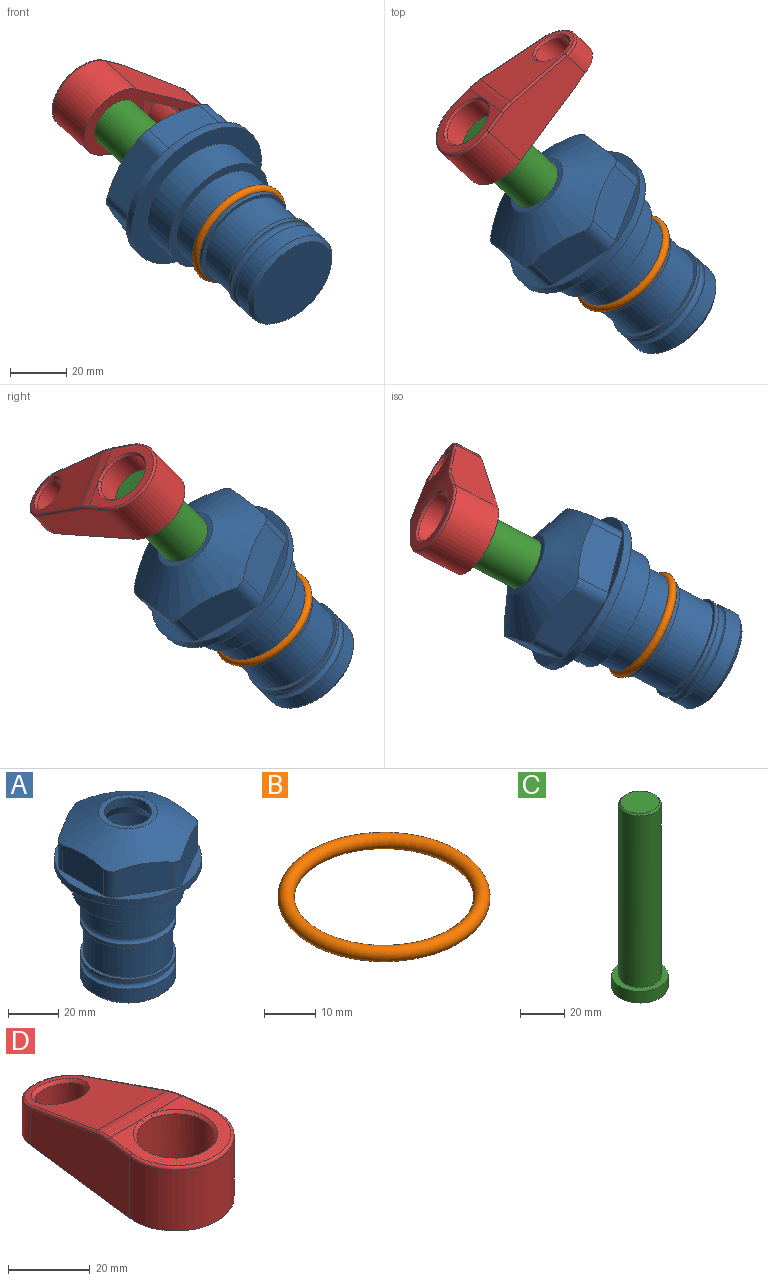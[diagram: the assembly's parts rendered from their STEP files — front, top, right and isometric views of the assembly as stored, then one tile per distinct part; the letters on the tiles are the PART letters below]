
ASSEMBLY  parts=4 mates=3
PART A: 36 faces, bbox 58.7x58.7x81 mm
  f0: cylinder r=17.78mm len=35.56mm, axis (0,0,1), area 1670.8mm2, adj f23,f24,f31
  f1: cylinder r=19.05mm len=38.1mm, axis (0,0,1), area 1191.9mm2, adj f26,f27,f30
  f2: plane 58.66x58.66mm, normal (0,0,-1), area 1150.6mm2, adj f3,f28
  f3: cylinder r=29.33mm len=58.66mm, axis (0,0,-1), area 585.1mm2, adj f2,f4
  f4: plane 58.66x58.66mm, normal (0,0,1), area 475.9mm2, adj f3,f5,f6,f7,f8,f9,f10,f11
  f5: plane 20.32x14.34mm, normal (-0.5,0.87,0), area 324.4mm2, adj f4,f15,f16,f17
  f6: plane 20.32x14.34mm, normal (0.5,0.87,0), area 324.4mm2, adj f4,f14,f15,f17
  f7: plane 23.48x14.34mm, normal (1,0,0), area 324.4mm2, adj f4,f13,f14,f17
  f8: plane 20.32x14.34mm, normal (0.5,-0.87,0), area 324.4mm2, adj f4,f12,f13,f17
  f9: plane 20.32x14.34mm, normal (-0.5,-0.87,0), area 324.4mm2, adj f4,f11,f12,f17
  f10: plane 23.48x14.34mm, normal (-1,0,0), area 324.4mm2, adj f4,f11,f16,f17
  f11: cylinder r=5.08mm len=12.85mm, axis (0,0,-1), area 67.2mm2, adj f4,f9,f10,f17
  f12: cylinder r=5.08mm len=12.85mm, axis (0,0,-1), area 67.2mm2, adj f4,f8,f9,f17
  f13: cylinder r=5.08mm len=12.85mm, axis (0,0,-1), area 67.2mm2, adj f4,f7,f8,f17
  f14: cylinder r=5.08mm len=12.85mm, axis (0,0,-1), area 67.2mm2, adj f4,f6,f7,f17
  f15: cylinder r=5.08mm len=12.85mm, axis (0,0,-1), area 67.2mm2, adj f4,f5,f6,f17
  f16: cylinder r=5.08mm len=12.85mm, axis (0,0,-1), area 67.2mm2, adj f4,f5,f10,f17
  f17: cone r=11.73mm half-angle=60deg, axis (0,0,-1), area 2071.8mm2, adj f5,f6,f7,f8,f9,f10,f11,f12
  f18: plane 23.46x23.46mm, normal (0,0,1), area 147.4mm2, adj f17,f35
  f19: plane 34.93x34.93mm, normal (0,0,-1), area 958mm2, adj f29
  f20: cylinder r=19.05mm len=38.1mm, axis (0,0,1), area 760.1mm2, adj f21,f29
  f21: torus R=19.05mm, axis (0,0,1), area 565.3mm2, adj f20,f22
  f22: cylinder r=19.05mm len=38.1mm, axis (0,0,1), area 190mm2, adj f21,f23
  f23: plane 38.1x38.1mm, normal (0,0,1), area 146.9mm2, adj f0,f22
  f24: plane 38.1x38.1mm, normal (0,0,-1), area 146.9mm2, adj f0,f25
  f25: cylinder r=19.05mm len=38.1mm, axis (0,0,1), area 190mm2, adj f24,f26
  f26: torus R=19.05mm, axis (0,0,1), area 565.3mm2, adj f1,f25
  f27: plane 44.45x44.45mm, normal (0,0,-1), area 411.7mm2, adj f1,f28
  f28: cylinder r=22.23mm len=44.45mm, axis (0,0,1), area 1773.5mm2, adj f2,f27
  f29: cone r=19.05mm half-angle=45deg, axis (0,0,1), area 257.5mm2, adj f19,f20
  f30: cylinder r=3.17mm len=6.75mm, axis (-1,0,0), area 128mm2, adj f1,f33
  f31: cylinder r=3.17mm len=6.35mm, axis (-1,0,0), area 102.5mm2, adj f0,f33
  f32: plane 25.4x25.4mm, normal (0,0,1), area 506.7mm2, adj f33
  f33: cylinder r=12.7mm len=66.42mm, axis (0,0,-1), area 5236.2mm2, adj f30,f31,f32,f34
  f34: cone r=9.53mm half-angle=30deg, axis (0,0,-1), area 443.4mm2, adj f33,f35
  f35: cylinder r=9.53mm len=19.05mm, axis (0,0,-1), area 240.9mm2, adj f18,f34
PART B: 1 faces, bbox 44.7x44.7x3.2 mm
  f0: torus R=19.05mm, axis (0,0,1), area 1193.9mm2
PART C: 6 faces, bbox 25.4x25.4x101.6 mm
  f0: plane 17.46x17.46mm, normal (0,0,1), area 239.5mm2, adj f5
  f1: plane 25.4x25.4mm, normal (0,0,-1), area 506.7mm2, adj f2
  f2: cylinder r=12.7mm len=25.4mm, axis (0,0,1), area 506.7mm2, adj f1,f3
  f3: plane 25.4x25.4mm, normal (0,0,1), area 221.7mm2, adj f2,f4
  f4: cylinder r=9.53mm len=94.46mm, axis (0,0,1), area 5653mm2, adj f3,f5
  f5: cone r=8.73mm half-angle=45deg, axis (0,0,-1), area 64.4mm2, adj f0,f4
PART D: 31 faces, bbox 31.7x65.5x19.8 mm
  f0: plane 39.12x18.26mm, normal (0.99,0.12,0), area 612.2mm2, adj f1,f4,f7,f11,f13,f15
  f1: cylinder r=9.53mm len=18.91mm, axis (0,0,-1), area 296.1mm2, adj f0,f2,f7,f17
  f2: plane 39.12x18.26mm, normal (-0.99,0.12,0), area 612.2mm2, adj f1,f4,f7,f12,f14,f16
  f3: cylinder r=6.35mm len=12.7mm, axis (0,0,-1), area 362.4mm2, adj f7,f18
  f4: cylinder r=14.29mm len=28.58mm, axis (0,0,-1), area 882.2mm2, adj f0,f2,f7,f10
  f5: cylinder r=9.53mm len=19.05mm, axis (0,0,-1), area 1092.6mm2, adj f7,f19,f20
  f6: plane 26.99x23.69mm, normal (0,0,1), area 216.2mm2, adj f9,f10,f11,f12,f19
  f7: plane 63.5x28.58mm, normal (0,0,-1), area 661.8mm2, adj f0,f1,f2,f3,f4,f5,f22,f23
  f8: plane 33.52x23.6mm, normal (0,0.26,0.97), area 486mm2, adj f9,f15,f16,f17,f18
  f9: cylinder r=19.05mm len=24.72mm, axis (1,0,0), area 120.4mm2, adj f6,f8,f13,f14,f20
  f10: torus R=13.49mm, axis (0,0,1), area 59mm2, adj f4,f6,f11,f12
  f11: cylinder r=0.79mm len=8.67mm, axis (0.12,-0.99,0), area 10.8mm2, adj f0,f6,f10,f13
  f12: cylinder r=0.79mm len=8.67mm, axis (0.12,0.99,0), area 10.8mm2, adj f2,f6,f10,f14
  f13: bspline ~4.95x1.42mm, area 6.1mm2, adj f0,f9,f11,f15
  f14: bspline ~4.95x1.42mm, area 6.1mm2, adj f2,f9,f12,f16
  f15: cylinder r=0.79mm len=25.95mm, axis (0.12,-0.96,0.26), area 32.9mm2, adj f0,f8,f13,f17
  f16: cylinder r=0.79mm len=25.95mm, axis (0.12,0.96,-0.26), area 32.9mm2, adj f2,f8,f14,f17
  f17: bspline ~18.91x8.38mm, area 30mm2, adj f1,f8,f15,f16
  f18: bspline ~14.29x14.29mm, area 48.3mm2, adj f3,f8
  f19: cone r=9.53mm half-angle=45deg, axis (0,0,1), area 66.5mm2, adj f5,f6,f20
  f20: bspline ~3.22x0.96mm, area 3.5mm2, adj f5,f9,f19
  f21: plane 2.75x2.72mm, normal (0,0,-1), area 2.9mm2, adj f23,f25,f28
  f22: plane 23.05x15.88mm, normal (-0.99,-0.12,0), area 323.6mm2, adj f7,f25,f26,f27,f28,f29
  f23: plane 23.05x15.88mm, normal (0.99,-0.12,0), area 323.6mm2, adj f7,f21,f25,f27,f28,f30
  f24: cylinder r=9.53mm len=10.69mm, axis (0,0,-1), area 114.7mm2, adj f7,f27,f29,f30
  f25: cylinder r=12.7mm len=20.59mm, axis (0,0,-1), area 381.1mm2, adj f7,f21,f22,f23,f26,f28
  f26: plane 2.75x2.72mm, normal (0,0,-1), area 2.9mm2, adj f22,f25,f28
  f27: plane 19.72x18.37mm, normal (0,-0.26,-0.97), area 291.8mm2, adj f22,f23,f24,f28,f29,f30
  f28: cylinder r=15.88mm len=19.92mm, axis (1,0,0), area 54.8mm2, adj f21,f22,f23,f25,f26,f27
  f29: cylinder r=1.59mm len=11mm, axis (0,0,-1), area 34.7mm2, adj f7,f22,f24,f27
  f30: cylinder r=1.59mm len=11mm, axis (0,0,-1), area 34.7mm2, adj f7,f23,f24,f27
PLACE A rot(axis=(-0.72,-0.29,0.63),74.5deg) t=(-44.81,-81.24,52.01)mm
PLACE B rot(axis=(-0.72,-0.29,0.63),74.5deg) t=(-44.81,-81.24,52.01)mm
PLACE C rot(axis=(-0.72,-0.29,0.63),74.5deg) t=(-40.86,-84.81,48.43)mm
PLACE D rot(axis=(-0.33,-0.78,-0.53),67.3deg) t=(-46.34,-79.86,53.39)mm
MATE cylindrical D.f4 <-> C.f2  axis (-0.62,0.56,0.56) through (-85.44,-44.49,88.79)mm
MATE fastened A.f0 <-> C.f2  axis (-0.62,0.56,0.56) through (-17.4,-106.03,27.2)mm
MATE fastened B.f0 <-> A.f0  axis (-0.62,0.56,0.56) through (-29.72,-94.89,38.35)mm
